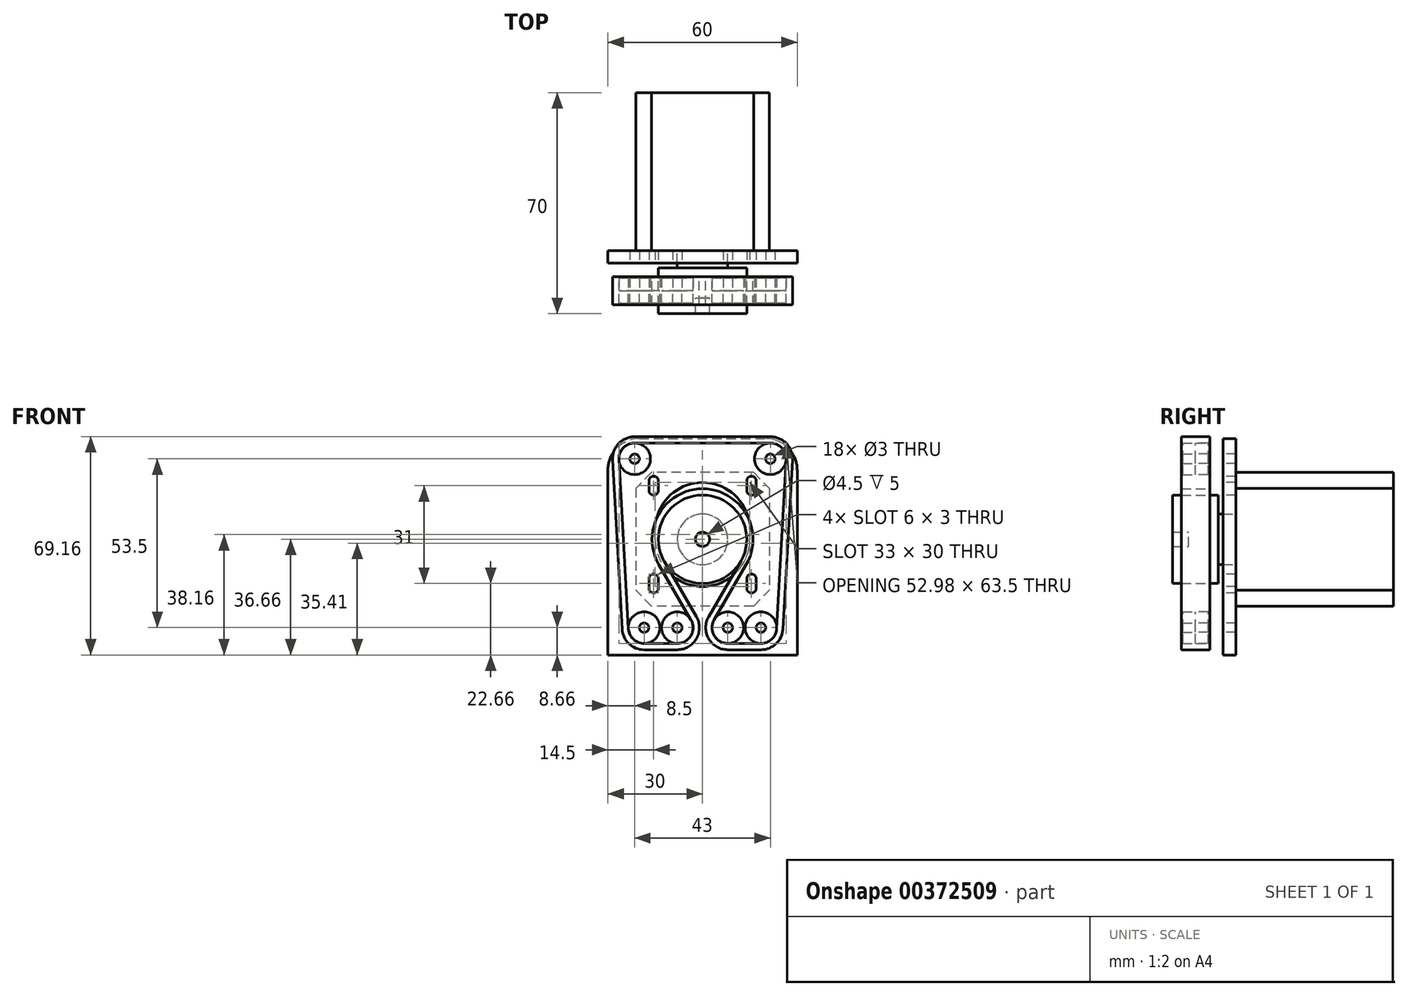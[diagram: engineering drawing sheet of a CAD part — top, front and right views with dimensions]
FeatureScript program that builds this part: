
annotation { "Feature Type Name" : "Feature", "Feature Type Description" : "" }
export const myFeature = defineFeature(function(context is Context, id is Id, definition is map)
    precondition{}
    {
        {
            var Q0;
            Q0=qCreatedBy(makeId("Front.planeOp"),FACE);
            var sketch = newSketch(context, id + "F0", { "sketchPlane" : qUnion([Q0])});
            skLineSegment(sketch, "E0", {"start": v(0, 0) * mm, "end": v(0, -33) * mm, "construction": true});
            skLineSegment(sketch, "E1", {"start": v(0, -33) * mm, "end": v(100, -33) * mm, "construction": true});
            skLineSegment(sketch, "E2.bottom", {"start": v(-21.5, 21.5) * mm, "end": v(21.5, 21.5) * mm, "construction": true});
            skLineSegment(sketch, "E2.top", {"start": v(-21.5, -21.5) * mm, "end": v(21.5, -21.5) * mm, "construction": true});
            skLineSegment(sketch, "E2.left", {"start": v(-21.5, 21.5) * mm, "end": v(-21.5, -21.5) * mm, "construction": true});
            skLineSegment(sketch, "E2.right", {"start": v(21.5, 21.5) * mm, "end": v(21.5, -21.5) * mm, "construction": true});
            skPoint(sketch, "E2.middle", {"position": v(0, 0) * mm});
            skLineSegment(sketch, "E3.bottom", {"start": v(-15.5, 15.5) * mm, "end": v(15.5, 15.5) * mm, "construction": true});
            skLineSegment(sketch, "E3.top", {"start": v(-15.5, -15.5) * mm, "end": v(15.5, -15.5) * mm, "construction": true});
            skLineSegment(sketch, "E3.left", {"start": v(-15.5, 15.5) * mm, "end": v(-15.5, -15.5) * mm, "construction": true});
            skLineSegment(sketch, "E3.right", {"start": v(15.5, 15.5) * mm, "end": v(15.5, -12.5) * mm, "construction": true});
            skLineSegment(sketch, "E4", {"start": v(12.71, -5.87) * mm, "end": v(3.46, -25.9) * mm, "construction": true});
            skLineSegment(sketch, "E5", {"start": v(0, 0) * mm, "end": v(0, 14) * mm, "construction": true});
            skCircle(sketch, "E6", {"center": v(8, -28) * mm, "radius": 1.5 * mm});
            skLineSegment(sketch, "E7", {"start": v(8, -28) * mm, "end": v(8, -26.5) * mm, "construction": true});
            skLineSegment(sketch, "E8", {"start": v(8, -26.5) * mm, "end": v(8, -21.5) * mm, "construction": true});
            skCircle(sketch, "E9", {"center": v(18.5, -28) * mm, "radius": 5 * mm, "construction": true});
            skLineSegment(sketch, "E10", {"start": v(8, -28) * mm, "end": v(18.5, -28) * mm, "construction": true});
            skLineSegment(sketch, "E11", {"start": v(8, -28) * mm, "end": v(3, -28) * mm, "construction": true});
            skLineSegment(sketch, "E12", {"start": v(3, -28) * mm, "end": v(0, -28) * mm, "construction": true});
            skCircle(sketch, "E13", {"center": v(18.5, -28) * mm, "radius": 1.5 * mm});
            skCircle(sketch, "E14", {"center": v(0, 0) * mm, "radius": 15 * mm});
            skLineSegment(sketch, "E15", {"start": v(15.5, -12.5) * mm, "end": v(15.5, -15.5) * mm, "construction": true});
            skLineSegment(sketch, "E16", {"start": v(15.5, 15.5) * mm, "end": v(15.5, 18.5) * mm, "construction": true});
            skArc(sketch, "E17.0.startCap", {"start": v(17, 15.5) * mm, "mid": v(15.5, 14) * mm, "end": v(14, 15.5) * mm});
            skArc(sketch, "E17.0.endCap", {"start": v(14, 18.5) * mm, "mid": v(15.5, 20) * mm, "end": v(17, 18.5) * mm});
            skLineSegment(sketch, "E17.0.left", {"start": v(14, 15.5) * mm, "end": v(14, 18.5) * mm});
            skLineSegment(sketch, "E17.0.right", {"start": v(17, 15.5) * mm, "end": v(17, 18.5) * mm});
            skArc(sketch, "E17.1.startCap", {"start": v(14, -12.5) * mm, "mid": v(15.5, -11) * mm, "end": v(17, -12.5) * mm});
            skArc(sketch, "E17.1.endCap", {"start": v(17, -15.5) * mm, "mid": v(15.5, -17) * mm, "end": v(14, -15.5) * mm});
            skLineSegment(sketch, "E17.1.left", {"start": v(17, -12.5) * mm, "end": v(17, -15.5) * mm});
            skLineSegment(sketch, "E17.1.right", {"start": v(14, -12.5) * mm, "end": v(14, -15.5) * mm});
            skArc(sketch, "E18.MirrorCS", {"start": v(-14, 18.5) * mm, "mid": v(-15.5, 20) * mm, "end": v(-17, 18.5) * mm});
            skLineSegment(sketch, "E19.MirrorCS", {"start": v(-14, 15.5) * mm, "end": v(-14, 18.5) * mm});
            skArc(sketch, "E20.MirrorCS", {"start": v(-17, 15.5) * mm, "mid": v(-15.5, 14) * mm, "end": v(-14, 15.5) * mm});
            skLineSegment(sketch, "E21.MirrorCS", {"start": v(-17, 15.5) * mm, "end": v(-17, 18.5) * mm});
            skArc(sketch, "E22.MirrorCS", {"start": v(-14, -12.5) * mm, "mid": v(-15.5, -11) * mm, "end": v(-17, -12.5) * mm});
            skLineSegment(sketch, "E23.MirrorCS", {"start": v(-14, -12.5) * mm, "end": v(-14, -15.5) * mm});
            skArc(sketch, "E24.MirrorCS", {"start": v(-17, -15.5) * mm, "mid": v(-15.5, -17) * mm, "end": v(-14, -15.5) * mm});
            skLineSegment(sketch, "E25.MirrorCS", {"start": v(-17, -12.5) * mm, "end": v(-17, -15.5) * mm});
            skCircle(sketch, "E26.MirrorC", {"center": v(-8, -28) * mm, "radius": 1.5 * mm});
            skCircle(sketch, "E27.MirrorC", {"center": v(-18.5, -28) * mm, "radius": 1.5 * mm});
            skCircle(sketch, "E28.MirrorC", {"center": v(-8, -28) * mm, "radius": 5 * mm, "construction": true});
            skCircle(sketch, "E29.MirrorC", {"center": v(-18.5, -28) * mm, "radius": 5 * mm, "construction": true});
            skLineSegment(sketch, "E30.MirrorCS", {"start": v(0, -33) * mm, "end": v(-100, -33) * mm, "construction": true});
            skArc(sketch, "E31", {"start": v(8, -33) * mm, "mid": v(12.21, -25.3) * mm, "end": v(3.46, -25.9) * mm, "construction": true});
            skArc(sketch, "E32", {"start": v(3.46, -25.9) * mm, "mid": v(3.79, -30.7) * mm, "end": v(8, -33) * mm, "construction": true});
            skArc(sketch, "E33", {"start": v(0, 14) * mm, "mid": v(-11.8, -7.54) * mm, "end": v(12.71, -5.87) * mm, "construction": true});
            skArc(sketch, "E34", {"start": v(12.71, -5.87) * mm, "mid": v(11.8, 7.54) * mm, "end": v(0, 14) * mm, "construction": true});
            skLineSegment(sketch, "E35.bottom", {"start": v(-30, 31.89) * mm, "end": v(30, 31.89) * mm});
            skLineSegment(sketch, "E35.top", {"start": v(-30, -36.66) * mm, "end": v(30, -36.66) * mm});
            skLineSegment(sketch, "E35.left", {"start": v(-30, 31.89) * mm, "end": v(-30, -36.66) * mm});
            skLineSegment(sketch, "E35.right", {"start": v(30, 31.89) * mm, "end": v(30, -36.66) * mm});
            skLineSegment(sketch, "E36", {"start": v(0, 0) * mm, "end": v(42.34, 0) * mm, "construction": true});
            skLineSegment(sketch, "E37", {"start": v(0, 14) * mm, "end": v(0, 31.89) * mm, "construction": true});
            skCircle(sketch, "E38", {"center": v(0, 3) * mm, "radius": 15 * mm});
            skLineSegment(sketch, "E39", {"start": v(-15, 0) * mm, "end": v(-15, 3) * mm});
            skLineSegment(sketch, "E40", {"start": v(15, 3) * mm, "end": v(15, 0) * mm});
            skLineSegment(sketch, "E41", {"start": v(20, -28) * mm, "end": v(30, -28) * mm, "construction": true});
            skCircle(sketch, "E42", {"center": v(-21.5, 25.5) * mm, "radius": 1.5 * mm});
            skCircle(sketch, "E43.MirrorC", {"center": v(21.5, 25.5) * mm, "radius": 1.5 * mm});
            skSolve(sketch);
        }
        {
            var Q0;
            Q0 = qSketchRegion(id + "F0", true);
            extrude(context, id + "F1", {"entities" : qUnion([Q0]), "oppositeDirection" : true, "depth" : 4 * mm});
        }
        {
            var Q0;
            Q0=makeQuery(id+"F1.opExtrude","CAP_FACE",FACE,{"disambiguationData":[OSD([sQuery(id+"F0.wireOp",EDGE,"E6"),sQuery(id+"F0.wireOp",EDGE,"E13"),sQuery(id+"F0.wireOp",EDGE,"E14"),sQuery(id+"F0.wireOp",EDGE,"E17.0.startCap"),sQuery(id+"F0.wireOp",EDGE,"E17.0.endCap"),sQuery(id+"F0.wireOp",EDGE,"E17.0.left"),sQuery(id+"F0.wireOp",EDGE,"E17.0.right"),sQuery(id+"F0.wireOp",EDGE,"E17.1.startCap"),sQuery(id+"F0.wireOp",EDGE,"E17.1.endCap"),sQuery(id+"F0.wireOp",EDGE,"E17.1.left"),sQuery(id+"F0.wireOp",EDGE,"E17.1.right"),sQuery(id+"F0.wireOp",EDGE,"E18.MirrorCS"),sQuery(id+"F0.wireOp",EDGE,"E19.MirrorCS"),sQuery(id+"F0.wireOp",EDGE,"E20.MirrorCS"),sQuery(id+"F0.wireOp",EDGE,"E21.MirrorCS"),sQuery(id+"F0.wireOp",EDGE,"E22.MirrorCS"),sQuery(id+"F0.wireOp",EDGE,"E23.MirrorCS"),sQuery(id+"F0.wireOp",EDGE,"E24.MirrorCS"),sQuery(id+"F0.wireOp",EDGE,"E25.MirrorCS"),sQuery(id+"F0.wireOp",EDGE,"E26.MirrorC"),sQuery(id+"F0.wireOp",EDGE,"E27.MirrorC"),sQuery(id+"F0.wireOp",EDGE,"E35.bottom"),sQuery(id+"F0.wireOp",EDGE,"E35.top"),sQuery(id+"F0.wireOp",EDGE,"E35.left"),sQuery(id+"F0.wireOp",EDGE,"E35.right")])],"isStart":false});
            var sketch = newSketch(context, id + "F2", { "sketchPlane" : qUnion([Q0])});
            skLineSegment(sketch, "E44.bottom", {"start": v(-21.15, 21.15) * mm, "end": v(21.15, 21.15) * mm});
            skLineSegment(sketch, "E44.top", {"start": v(-21.15, -21.15) * mm, "end": v(21.15, -21.15) * mm});
            skLineSegment(sketch, "E44.left", {"start": v(-21.15, 21.15) * mm, "end": v(-21.15, -21.15) * mm});
            skLineSegment(sketch, "E44.right", {"start": v(21.15, 21.15) * mm, "end": v(21.15, -21.15) * mm});
            skPoint(sketch, "E44.middle", {"position": v(0, 0) * mm});
            skSolve(sketch);
        }
        {
            var Q0;
            Q0 = qSketchRegion(id + "F2", true);
            extrude(context, id + "F3", {"entities" : qUnion([Q0]), "depth" : 50 * mm});
        }
        {
            var Q0;
            Q0=makeQuery(id+"F3.opExtrude","SWEPT_EDGE",EDGE,{"disambiguationData":[OSD([sQuery(id+"F2.wireOp",EDGE,"E44.bottom"),sQuery(id+"F2.wireOp",EDGE,"E44.right")])]});
            var Q1;
            Q1=makeQuery(id+"F3.opExtrude","SWEPT_EDGE",EDGE,{"disambiguationData":[OSD([sQuery(id+"F2.wireOp",EDGE,"E44.bottom"),sQuery(id+"F2.wireOp",EDGE,"E44.left")])]});
            var Q2;
            Q2=makeQuery(id+"F3.opExtrude","SWEPT_EDGE",EDGE,{"disambiguationData":[OSD([sQuery(id+"F2.wireOp",EDGE,"E44.top"),sQuery(id+"F2.wireOp",EDGE,"E44.right")])]});
            var Q3;
            Q3=makeQuery(id+"F3.opExtrude","SWEPT_EDGE",EDGE,{"disambiguationData":[OSD([sQuery(id+"F2.wireOp",EDGE,"E44.top"),sQuery(id+"F2.wireOp",EDGE,"E44.left")])]});
            chamfer(context, id + "F4", {"entities" : qUnion([Q0, Q1, Q2, Q3]), "width" : 5 * mm, "tangentPropagation" : true});
        }
        {
            var Q0;
            Q0=makeQuery(id+"F3.opExtrude","CAP_FACE",FACE,{"disambiguationData":[OSD([sQuery(id+"F2.wireOp",EDGE,"E44.bottom"),sQuery(id+"F2.wireOp",EDGE,"E44.top"),sQuery(id+"F2.wireOp",EDGE,"E44.left"),sQuery(id+"F2.wireOp",EDGE,"E44.right")])],"isStart":true});
            var sketch = newSketch(context, id + "F5", { "sketchPlane" : qUnion([Q0])});
            skCircle(sketch, "E45", {"center": v(0, 0) * mm, "radius": 2.25 * mm});
            skSolve(sketch);
        }
        {
            var Q0;
            Q0 = qSketchRegion(id + "F5", true);
            extrude(context, id + "F6", {"entities" : qUnion([Q0]), "operationType" : NewBodyOperationType.ADD, "depth" : 15 * mm});
        }
        {
            var Q0;
            Q0=makeQuery(id+"F3.opExtrude","CAP_FACE",FACE,{"disambiguationData":[OSD([sQuery(id+"F2.wireOp",EDGE,"E44.bottom"),sQuery(id+"F2.wireOp",EDGE,"E44.top"),sQuery(id+"F2.wireOp",EDGE,"E44.left"),sQuery(id+"F2.wireOp",EDGE,"E44.right")])],"isStart":true});
            cPlane(context, id + "F7", {"entities" : qUnion([Q0]), "cplaneType" : CPlaneType.OFFSET, "offset" : 0 * mm, "width" : 150 * mm, "height" : 150 * mm});
        }
        {
            var Q0;
            Q0=qCreatedBy(id+"F7.planeOp",FACE);
            var sketch = newSketch(context, id + "F8", { "sketchPlane" : qUnion([Q0])});
            skCircle(sketch, "E46", {"center": v(0, 0) * mm, "radius": 8 * mm});
            skCircle(sketch, "E47.0", {"center": v(0, 0) * mm, "radius": 2.25 * mm});
            skSolve(sketch);
        }
        {
            var Q0;
            Q0 = qSketchRegion(id + "F8", true);
            extrude(context, id + "F9", {"entities" : qUnion([Q0]), "depth" : 5.5 * mm});
        }
        {
            var Q0;
            Q0=makeQuery(id+"F9.opExtrude","CAP_FACE",FACE,{"disambiguationData":[OSD([sQuery(id+"F8.wireOp",EDGE,"E46"),sQuery(id+"F8.wireOp",EDGE,"E47.0")])],"isStart":false});
            var sketch = newSketch(context, id + "F10", { "sketchPlane" : qUnion([Q0])});
            skCircle(sketch, "E48", {"center": v(0, 0) * mm, "radius": 14 * mm});
            skCircle(sketch, "E49.0", {"center": v(0, 0) * mm, "radius": 2.25 * mm});
            skSolve(sketch);
        }
        {
            var Q0;
            Q0 = qSketchRegion(id + "F10", true);
            extrude(context, id + "F11", {"entities" : qUnion([Q0]), "operationType" : NewBodyOperationType.ADD, "depth" : 14.5 * mm});
        }
        {
            var Q0;
            Q0=makeQuery(id+"F11.opExtrude","CAP_FACE",FACE,{"disambiguationData":[OSD([sQuery(id+"F10.wireOp",EDGE,"E48"),sQuery(id+"F10.wireOp",EDGE,"E49.0")])],"isStart":false});
            var Q1;
            Q1=makeQuery(id+"F11.opExtrude","CAP_FACE",FACE,{"disambiguationData":[OSD([sQuery(id+"F10.wireOp",EDGE,"E48"),sQuery(id+"F10.wireOp",EDGE,"E49.0")])],"isStart":true});
            cPlane(context, id + "F12", {"entities" : qUnion([Q0, Q1]), "cplaneType" : CPlaneType.MID_PLANE, "offset" : 25 * mm, "width" : 150 * mm, "height" : 150 * mm});
        }
        {
            var Q0;
            Q0=qCreatedBy(id+"F12.planeOp",FACE);
            var sketch = newSketch(context, id + "F13", { "sketchPlane" : qUnion([Q0])});
            skCircle(sketch, "E50.0", {"center": v(-18.5, -28) * mm, "radius": 1.5 * mm});
            skCircle(sketch, "E50.1", {"center": v(-8, -28) * mm, "radius": 1.5 * mm});
            skCircle(sketch, "E50.2", {"center": v(8, -28) * mm, "radius": 1.5 * mm});
            skCircle(sketch, "E50.3", {"center": v(18.5, -28) * mm, "radius": 1.5 * mm});
            skCircle(sketch, "E51", {"center": v(-18.5, -28) * mm, "radius": 5 * mm});
            skCircle(sketch, "E52", {"center": v(-8, -28) * mm, "radius": 5 * mm});
            skCircle(sketch, "E53", {"center": v(8, -28) * mm, "radius": 5 * mm});
            skCircle(sketch, "E54", {"center": v(18.5, -28) * mm, "radius": 5 * mm});
            skCircle(sketch, "E55.0", {"center": v(21.5, 25.5) * mm, "radius": 1.5 * mm});
            skCircle(sketch, "E55.1", {"center": v(-21.5, 25.5) * mm, "radius": 1.5 * mm});
            skCircle(sketch, "E56", {"center": v(-21.5, 25.5) * mm, "radius": 5 * mm});
            skCircle(sketch, "E57", {"center": v(21.5, 25.5) * mm, "radius": 5 * mm});
            skSolve(sketch);
        }
        {
            var Q0;
            Q0 = qSketchRegion(id + "F13", true);
            extrude(context, id + "F14", {"entities" : qUnion([Q0]), "depth" : 4 * mm});
        }
        {
            var Q0;
            Q0=makeQuery(id+"F14.opExtrude","CAP_FACE",FACE,{"disambiguationData":[OSD([sQuery(id+"F13.wireOp",EDGE,"E50.3"),sQuery(id+"F13.wireOp",EDGE,"E54")])],"isStart":true});
            var Q1;
            Q1=makeQuery(id+"F14.opExtrude","CAP_FACE",FACE,{"disambiguationData":[OSD([sQuery(id+"F13.wireOp",EDGE,"E50.2"),sQuery(id+"F13.wireOp",EDGE,"E53")])],"isStart":true});
            var Q2;
            Q2=makeQuery(id+"F14.opExtrude","CAP_FACE",FACE,{"disambiguationData":[OSD([sQuery(id+"F13.wireOp",EDGE,"E50.1"),sQuery(id+"F13.wireOp",EDGE,"E52")])],"isStart":true});
            var Q3;
            Q3=makeQuery(id+"F14.opExtrude","CAP_FACE",FACE,{"disambiguationData":[OSD([sQuery(id+"F13.wireOp",EDGE,"E50.0"),sQuery(id+"F13.wireOp",EDGE,"E51")])],"isStart":true});
            var Q4;
            Q4=makeQuery(id+"F14.opExtrude","CAP_FACE",FACE,{"disambiguationData":[OSD([sQuery(id+"F13.wireOp",EDGE,"E55.1"),sQuery(id+"F13.wireOp",EDGE,"E56")])],"isStart":true});
            var Q5;
            Q5=makeQuery(id+"F14.opExtrude","CAP_FACE",FACE,{"disambiguationData":[OSD([sQuery(id+"F13.wireOp",EDGE,"E55.0"),sQuery(id+"F13.wireOp",EDGE,"E57")])],"isStart":true});
            extrude(context, id + "F15", {"entities" : qUnion([Q0, Q1, Q2, Q3, Q4, Q5]), "depth" : 4 * mm});
        }
        {
            var Q0;
            Q0=qCreatedBy(id+"F12.planeOp",FACE);
            var sketch = newSketch(context, id + "F16", { "sketchPlane" : qUnion([Q0])});
            skLineSegment(sketch, "E58", {"start": v(0, 0) * mm, "end": v(0, 14) * mm, "construction": true});
            skLineSegment(sketch, "E59", {"start": v(12.1, -7.04) * mm, "end": v(1.95, -24.48) * mm});
            skLineSegment(sketch, "E60", {"start": v(8, -35) * mm, "end": v(18.5, -35) * mm});
            skLineSegment(sketch, "E61", {"start": v(8, -33) * mm, "end": v(18.5, -33) * mm});
            skArc(sketch, "E62", {"start": v(1.95, -24.48) * mm, "mid": v(1.93, -31.49) * mm, "end": v(8, -35) * mm});
            skArc(sketch, "E63", {"start": v(13.83, -8.05) * mm, "mid": v(13.87, 7.98) * mm, "end": v(0, 16) * mm});
            skLineSegment(sketch, "E64", {"start": v(0, 16) * mm, "end": v(0, 14) * mm, "construction": true});
            skLineSegment(sketch, "E65", {"start": v(3.68, -25.48) * mm, "end": v(13.83, -8.05) * mm});
            skArc(sketch, "E66", {"start": v(0, 14) * mm, "mid": v(-12.14, -6.98) * mm, "end": v(12.1, -7.04) * mm, "construction": true});
            skArc(sketch, "E67", {"start": v(12.1, -7.04) * mm, "mid": v(12.14, 6.98) * mm, "end": v(0, 14) * mm});
            skArc(sketch, "E68", {"start": v(3.68, -25.48) * mm, "mid": v(3.67, -30.5) * mm, "end": v(8, -33) * mm});
            skArc(sketch, "E69", {"start": v(8, -33) * mm, "mid": v(12.33, -25.5) * mm, "end": v(3.68, -25.48) * mm, "construction": true});
            skArc(sketch, "E70.MirrorCS", {"start": v(-13.83, -8.05) * mm, "mid": v(-13.87, 7.98) * mm, "end": v(0, 16) * mm});
            skArc(sketch, "E71.MirrorCS", {"start": v(-12.1, -7.04) * mm, "mid": v(-12.14, 6.98) * mm, "end": v(0, 14) * mm});
            skLineSegment(sketch, "E72.MirrorCS", {"start": v(-3.68, -25.48) * mm, "end": v(-13.83, -8.05) * mm});
            skLineSegment(sketch, "E73.MirrorCS", {"start": v(-12.1, -7.04) * mm, "end": v(-1.95, -24.48) * mm});
            skArc(sketch, "E74.MirrorCS", {"start": v(-1.95, -24.48) * mm, "mid": v(-1.93, -31.49) * mm, "end": v(-8, -35) * mm});
            skArc(sketch, "E75.MirrorCS", {"start": v(-3.68, -25.48) * mm, "mid": v(-3.67, -30.5) * mm, "end": v(-8, -33) * mm});
            skLineSegment(sketch, "E76", {"start": v(8, -33) * mm, "end": v(8, -35) * mm, "construction": true});
            skLineSegment(sketch, "E77", {"start": v(0, 16) * mm, "end": v(0, 32.5) * mm, "construction": true});
            skLineSegment(sketch, "E78", {"start": v(21.5, 30.5) * mm, "end": v(0, 30.5) * mm});
            skLineSegment(sketch, "E79", {"start": v(0, 32.5) * mm, "end": v(21.5, 32.5) * mm});
            skLineSegment(sketch, "E80", {"start": v(23.5, -28.28) * mm, "end": v(26.5, 25.22) * mm});
            skArc(sketch, "E81", {"start": v(23.5, -28.28) * mm, "mid": v(15.06, -24.37) * mm, "end": v(18.5, -33) * mm, "construction": true});
            skArc(sketch, "E82", {"start": v(18.5, -33) * mm, "mid": v(21.94, -31.63) * mm, "end": v(23.5, -28.28) * mm});
            skArc(sketch, "E83", {"start": v(18.5, -35) * mm, "mid": v(23.3, -33.09) * mm, "end": v(25.49, -28.4) * mm});
            skArc(sketch, "E84", {"start": v(21.5, 32.5) * mm, "mid": v(26.59, 30.3) * mm, "end": v(28.49, 25.1) * mm});
            skLineSegment(sketch, "E85", {"start": v(25.49, -28.4) * mm, "end": v(28.49, 25.1) * mm});
            skArc(sketch, "E86", {"start": v(21.5, 30.5) * mm, "mid": v(17.87, 22.06) * mm, "end": v(26.5, 25.22) * mm, "construction": true});
            skArc(sketch, "E87", {"start": v(26.5, 25.22) * mm, "mid": v(25.13, 28.94) * mm, "end": v(21.5, 30.5) * mm});
            skLineSegment(sketch, "E88.MirrorCS", {"start": v(0, 32.5) * mm, "end": v(-21.5, 32.5) * mm});
            skLineSegment(sketch, "E89.MirrorCS", {"start": v(-21.5, 30.5) * mm, "end": v(0, 30.5) * mm});
            skArc(sketch, "E90.MirrorCS", {"start": v(-21.5, 32.5) * mm, "mid": v(-26.59, 30.3) * mm, "end": v(-28.49, 25.1) * mm});
            skArc(sketch, "E91.MirrorCS", {"start": v(-26.5, 25.22) * mm, "mid": v(-25.13, 28.94) * mm, "end": v(-21.5, 30.5) * mm});
            skLineSegment(sketch, "E92.MirrorCS", {"start": v(-23.5, -28.28) * mm, "end": v(-26.5, 25.22) * mm});
            skLineSegment(sketch, "E93.MirrorCS", {"start": v(-25.49, -28.4) * mm, "end": v(-28.49, 25.1) * mm});
            skArc(sketch, "E94.MirrorCS", {"start": v(-18.5, -35) * mm, "mid": v(-23.3, -33.09) * mm, "end": v(-25.49, -28.4) * mm});
            skArc(sketch, "E95.MirrorCS", {"start": v(-18.5, -33) * mm, "mid": v(-21.94, -31.63) * mm, "end": v(-23.5, -28.28) * mm});
            skLineSegment(sketch, "E96.MirrorCS", {"start": v(-8, -33) * mm, "end": v(-18.5, -33) * mm});
            skLineSegment(sketch, "E97.MirrorCS", {"start": v(-8, -35) * mm, "end": v(-18.5, -35) * mm});
            skSolve(sketch);
        }
        {
            var Q0;
            Q0 = qSketchRegion(id + "F16", true);
            extrude(context, id + "F17", {"entities" : qUnion([Q0]), "depth" : 9 * mm, "symmetric" : true});
        }
        {
            var Q0;
            Q0=makeQuery(id+"F1.opExtrude","SWEPT_EDGE",EDGE,{"disambiguationData":[OSD([sQuery(id+"F0.wireOp",EDGE,"E35.bottom"),sQuery(id+"F0.wireOp",EDGE,"E35.left")])]});
            var Q1;
            Q1=makeQuery(id+"F1.opExtrude","SWEPT_EDGE",EDGE,{"disambiguationData":[OSD([sQuery(id+"F0.wireOp",EDGE,"E35.bottom"),sQuery(id+"F0.wireOp",EDGE,"E35.right")])]});
            fillet(context, id + "F18", {"entities" : qUnion([Q0, Q1]), "radius" : 10 * mm, "tangentPropagation" : true, "allowEdgeOverflow" : false});
        }
    });
